# Revit family: FU_Inspec_Grade_Plus_2-2
name_source: partatom
category: Furniture
units: mm (PartAtom-declared; Revit-internal decimal feet)

## family parameters
Always vertical = Yes
Cut with Voids When Loaded = No
OmniClass Number = 23.40.20.00
OmniClass Title = General Furniture and Specialties
Room Calculation Point = No
Shared = No
Work Plane-Based = No

## types (2) — shared parameters
Assembly Code = E2020
Depth = 550 mm
Height = 800 mm  [stored 2.62467 ft]
Keynote = 46.B
Manufacturer = Inspec
Seat Material = Plastic - White
Seat Pad Material = Colour - Khaki
URL = https://inspecfurniture.com
Weight = 5 kg
Width = 590 mm  [stored 1.9357 ft]
zero-valued in all types: Default Elevation

## per-type parameters (varying)
| type | Description | Frame Material | Model |
| Grade Plus 2.1 - Chrome - White | Armchair with recycled polypropylene seat on a powder coated or chromium plated tubular steel frame. | Metal - Chrome - Polished | Grade Plus 2.1 |
| Grade Plus 2.2 - White - White | Armchair with recycled polypropylene seat on a powder coated or chromium plated tubular steel frame with upholstered seat pad. | Metal - White - Matte | Grade Plus 2.2 |

note: [stored X ft] marks values corroborated as IEEE doubles in the binary element streams (Revit-internal decimal feet)

## geometry (parser evidence)
native form markers: Blend x2, Sweep x2
no freeform markers — native parametric forms only
